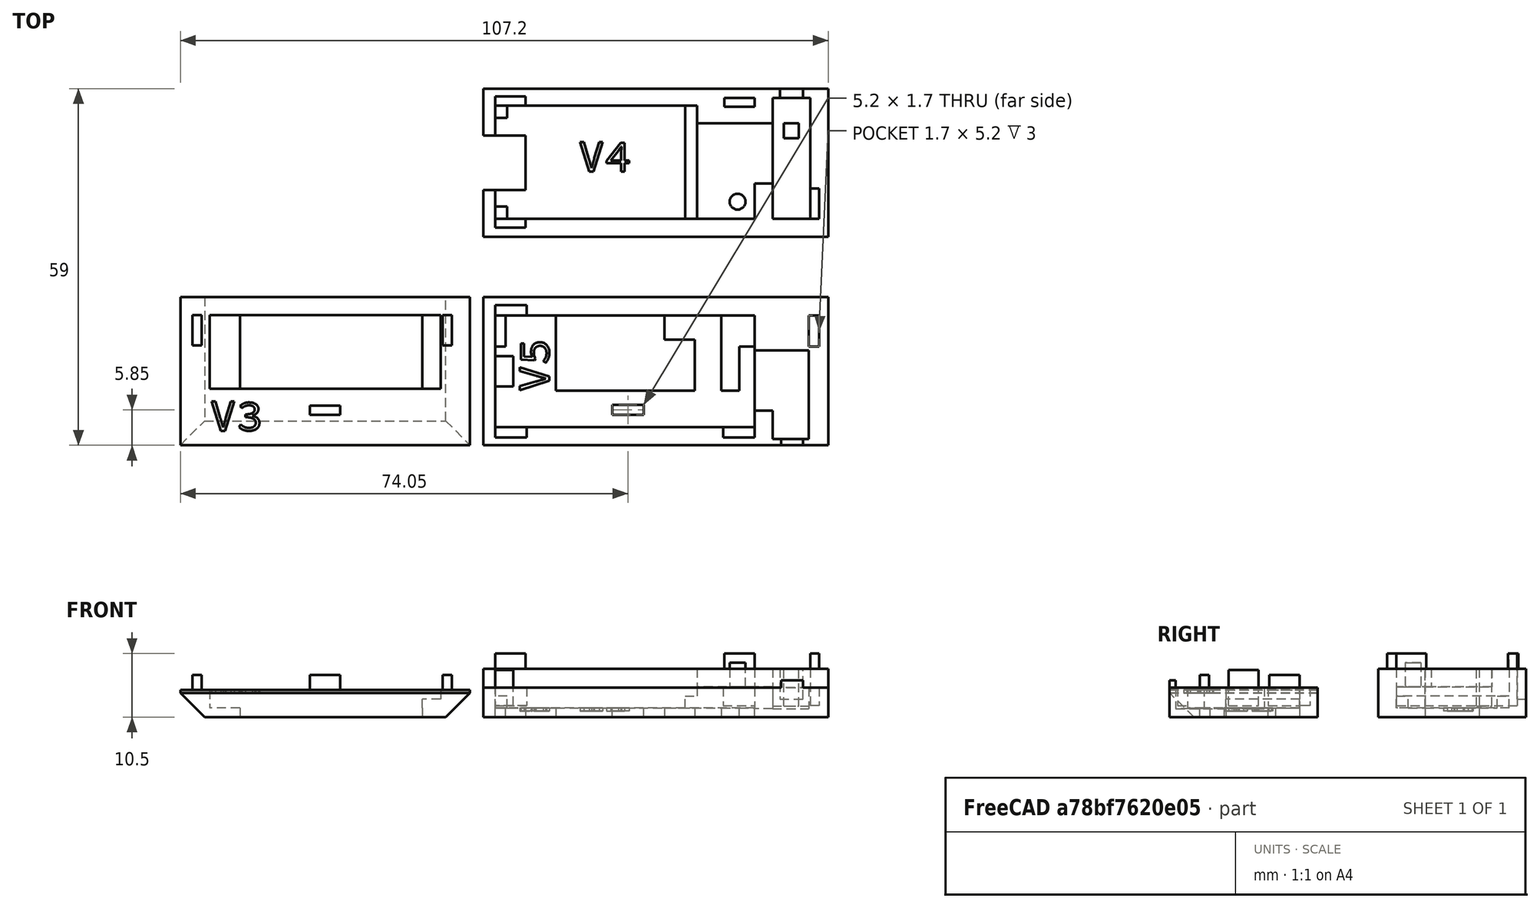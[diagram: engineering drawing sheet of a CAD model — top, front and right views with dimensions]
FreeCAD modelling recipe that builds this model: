
FCSTD DOCUMENT  (FreeCAD 0.18R16161 (Git))
Label: ppm_body
License: All rights reserved
LicenseURL: http://en.wikipedia.org/wiki/All_rights_reserved
objects: Sketcher::SketchObject×29, PartDesign::Pocket×15, PartDesign::Pad×14, App::MeasureDistance×7, Part::Part2DObjectPython×3, Part::Extrusion×3, PartDesign::Body×3, Part::Cut×3, Mesh::Feature×3, PartDesign::Chamfer×1
note: 100 computed .brp shape members not serialized (recipe doc carries the construction recipe); baked Part::Feature solids carry a one-line shape summary decoded from their .brp

FEATURE [Sketcher::SketchObject] Sketch  label="Case_Sketch"
  MapMode = 5
  Support = -> [XY_Plane]
  sketch-geometry (4):
    g0: LineSegment StartX=0 StartY=0 StartZ=0 EndX=47.9 EndY=0 EndZ=0
    g1: LineSegment StartX=47.9 StartY=0 StartZ=0 EndX=47.9 EndY=24.5 EndZ=0
    g2: LineSegment StartX=47.9 StartY=24.5 StartZ=0 EndX=0 EndY=24.5 EndZ=0
    g3: LineSegment StartX=0 StartY=24.5 StartZ=0 EndX=0 EndY=0 EndZ=0
  constraints (11):
    c: Coincident(g0,g1)
    c: Coincident(g1,g2)
    c: Coincident(g2,g3)
    c: Coincident(g3,g0)
    c: Horizontal(g0)
    c: Horizontal(g2)
    c: Vertical(g1)
    c: Vertical(g3)
    c: Coincident(g0,g-1)
    c: DistanceX(g0,g0) = 47.9
    c: DistanceY(g3,g3) = 24.5
FEATURE [PartDesign::Pad] Pad  label="Case"
  Length = 8
  Length2 = 100
  Profile = -> Sketch
  Type = 0
FEATURE [Sketcher::SketchObject] Sketch001  label="ProMicro_Skethc"
  ExternalGeometry = -> [Pad]
  MapMode = 5
  Placement = pos=(0,0,8) rot=(0,0,1;0rad)
  Support = -> [Pad]
  sketch-geometry (6):
    g0: LineSegment StartX=2 StartY=21.7 StartZ=0 EndX=35.4 EndY=21.7 EndZ=0
    g1: LineSegment StartX=35.4 StartY=21.7 StartZ=0 EndX=35.4 EndY=3 EndZ=0
    g2: LineSegment StartX=35.4 StartY=3 StartZ=0 EndX=2 EndY=3 EndZ=0
    g3: LineSegment StartX=2 StartY=3 StartZ=0 EndX=2 EndY=21.7 EndZ=0
    g4: LineSegment [constr] StartX=2 StartY=0 StartZ=0 EndX=2 EndY=3 EndZ=0
    g5: LineSegment [constr] StartX=0 StartY=3 StartZ=0 EndX=2 EndY=3 EndZ=0
  constraints (18):
    c: Coincident(g0,g1)
    c: Coincident(g1,g2)
    c: Coincident(g2,g3)
    c: Coincident(g3,g0)
    c: Horizontal(g0)
    c: Horizontal(g2)
    c: Vertical(g1)
    c: Vertical(g3)
    c: DistanceX(g2,g2) = 33.4
    c: DistanceY(g3,g3) = 18.7
    c: PointOnObject(g4,g-3)
    c: Vertical(g4)
    c: PointOnObject(g5,g-4)
    c: Horizontal(g5)
    c: DistanceX(g5,g5) = 2
    c: DistanceY(g4,g4) = 3
    c: Coincident(g5,g2)
    c: Coincident(g4,g2)
FEATURE [PartDesign::Pocket] Pocket  label="ProMicro"
  BaseFeature = -> Pad
  Length = 6.5
  Length2 = 100
  Profile = -> Sketch001
  Type = 0
FEATURE [Sketcher::SketchObject] Sketch002  label="USBHole"
  ExternalGeometry = -> [Pocket]
  MapMode = 5
  Placement = pos=(0,0,8) rot=(0,0,1;0rad)
  Support = -> [Pocket]
  sketch-geometry (6):
    g0: GeomPoint X=0 Y=12.25 Z=0
    g1: LineSegment StartX=0 StartY=16.75 StartZ=0 EndX=7 EndY=16.75 EndZ=0
    g2: LineSegment StartX=7 StartY=16.75 StartZ=0 EndX=7 EndY=7.75 EndZ=0
    g3: LineSegment StartX=7 StartY=7.75 StartZ=0 EndX=0 EndY=7.75 EndZ=0
    g4: LineSegment StartX=0 StartY=7.75 StartZ=0 EndX=0 EndY=16.75 EndZ=0
    g5: GeomPoint X=0 Y=12.25 Z=0
  constraints (13):
    c: Symmetric(g-3,g-3,g0)
    c: Coincident(g1,g2)
    c: Coincident(g2,g3)
    c: Coincident(g3,g4)
    c: Coincident(g4,g1)
    c: Horizontal(g1)
    c: Horizontal(g3)
    c: Vertical(g2)
    c: Vertical(g4)
    c: Symmetric(g4,g4,g5)
    c: Coincident(g5,g0)
    c: DistanceY(g4,g4) = 9
    c: DistanceX(g3,g3) = 7
FEATURE [PartDesign::Pocket] Pocket001  label="USBHole001"
  BaseFeature = -> Pocket
  Length = 8
  Length2 = 100
  Profile = -> Sketch002
  Type = 0
FEATURE [Sketcher::SketchObject] Sketch003  label="ProMicroRests"
  ExternalGeometry = -> [Pocket001]
  MapMode = 5
  Placement = pos=(0,0,1.5) rot=(0,0,1;0rad)
  Support = -> [Pocket001]
  sketch-geometry (12):
    g0: LineSegment StartX=35.4 StartY=21.7 StartZ=0 EndX=33.4 EndY=21.7 EndZ=0
    g1: LineSegment StartX=33.4 StartY=21.7 StartZ=0 EndX=33.4 EndY=3 EndZ=0
    g2: LineSegment StartX=33.4 StartY=3 StartZ=0 EndX=35.4 EndY=3 EndZ=0
    g3: LineSegment StartX=35.4 StartY=3 StartZ=0 EndX=35.4 EndY=21.7 EndZ=0
    g4: LineSegment StartX=2 StartY=5 StartZ=0 EndX=4 EndY=5 EndZ=0
    g5: LineSegment StartX=4 StartY=5 StartZ=0 EndX=4 EndY=3 EndZ=0
    g6: LineSegment StartX=4 StartY=3 StartZ=0 EndX=2 EndY=3 EndZ=0
    g7: LineSegment StartX=2 StartY=3 StartZ=0 EndX=2 EndY=5 EndZ=0
    g8: LineSegment StartX=4 StartY=21.7 StartZ=0 EndX=4 EndY=19.7 EndZ=0
    g9: LineSegment StartX=2 StartY=21.7 StartZ=0 EndX=4 EndY=21.7 EndZ=0
    g10: LineSegment StartX=4 StartY=19.7 StartZ=0 EndX=2 EndY=19.7 EndZ=0
    g11: LineSegment StartX=2 StartY=19.7 StartZ=0 EndX=2 EndY=21.7 EndZ=0
  constraints (32):
    c: Coincident(g0,g1)
    c: Coincident(g1,g2)
    c: Coincident(g2,g3)
    c: Coincident(g3,g0)
    c: Horizontal(g0)
    c: Horizontal(g2)
    c: Vertical(g1)
    c: DistanceX(g0,g0) = 2
    c: Coincident(g-5,g0)
    c: Coincident(g2,g-5)
    c: Coincident(g4,g5)
    c: Coincident(g5,g6)
    c: Coincident(g6,g7)
    c: Coincident(g7,g4)
    c: Horizontal(g4)
    c: Horizontal(g6)
    c: Vertical(g5)
    c: Vertical(g7)
    c: DistanceX(g4,g4) = 2
    c: Coincident(g-4,g6)
    c: DistanceY(g5,g5) = 2
    c: Coincident(g9,g8)
    c: Coincident(g8,g10)
    c: Coincident(g10,g11)
    c: Coincident(g11,g9)
    c: Horizontal(g9)
    c: Horizontal(g10)
    c: Vertical(g8)
    c: Vertical(g11)
    c: Equal(g4,g9) = 2
    c: Equal(g5,g8) = 2
    c: Coincident(g-3,g9)
FEATURE [PartDesign::Pad] Pad001  label="ProMicroRest"
  BaseFeature = -> Pocket001
  Length = 2
  Length2 = 100
  Profile = -> Sketch003
  Type = 0
FEATURE [Sketcher::SketchObject] Sketch004  label="MPUHole_Sketch"
  ExternalGeometry = -> [Pad001]
  MapMode = 5
  Placement = pos=(0,0,8) rot=(0,0,1;0rad)
  Support = -> [Pad001]
  sketch-geometry (5):
    g0: LineSegment StartX=35.4 StartY=18.8 StartZ=0 EndX=44.9 EndY=18.8 EndZ=0
    g1: LineSegment StartX=44.9 StartY=18.8 StartZ=0 EndX=44.9 EndY=3 EndZ=0
    g2: LineSegment StartX=44.9 StartY=3 StartZ=0 EndX=35.4 EndY=3 EndZ=0
    g3: LineSegment StartX=35.4 StartY=3 StartZ=0 EndX=35.4 EndY=18.8 EndZ=0
    g4: LineSegment [constr] StartX=44.9 StartY=3 StartZ=0 EndX=47.9 EndY=3 EndZ=0
  constraints (14):
    c: Coincident(g0,g1)
    c: Coincident(g1,g2)
    c: Coincident(g2,g3)
    c: Horizontal(g0)
    c: Horizontal(g2)
    c: Vertical(g1)
    c: Vertical(g3)
    c: DistanceY(g1,g1) = 15.8
    c: Coincident(g3,g0)
    c: Coincident(g-3,g2)
    c: Coincident(g4,g1)
    c: PointOnObject(g4,g-4)
    c: Horizontal(g4)
    c: DistanceX(g4,g4) = 3
FEATURE [PartDesign::Pocket] Pocket002  label="MPU_Hole"
  BaseFeature = -> Pad001
  Length = 3
  Length2 = 100
  Profile = -> Sketch004
  Type = 0
FEATURE [Sketcher::SketchObject] Sketch005  label="Pin_Sketch"
  ExternalGeometry = -> [Pocket002]
  MapMode = 5
  Placement = pos=(0,0,5) rot=(0,0,1;0rad)
  Support = -> [Pocket002]
  sketch-geometry (3):
    g0: LineSegment [constr] StartX=42.1 StartY=3 StartZ=0 EndX=42.1 EndY=5.8 EndZ=0
    g1: LineSegment [constr] StartX=44.9 StartY=5.8 StartZ=0 EndX=42.1 EndY=5.8 EndZ=0
    g2: Circle CenterX=42.1 CenterY=5.8 CenterZ=0 NormalX=0 NormalY=0 NormalZ=1 AngleXU=0 Radius=1.3
  constraints (9):
    c: PointOnObject(g0,g-3)
    c: Vertical(g0)
    c: PointOnObject(g1,g-4)
    c: Horizontal(g1)
    c: DistanceX(g1,g1) = 2.8
    c: DistanceY(g0,g0) = 2.8
    c: Coincident(g0,g1)
    c: Radius(g2) = 1.3
    c: Coincident(g2,g0)
FEATURE [PartDesign::Pad] Pad002  label="Pin"
  BaseFeature = -> Pocket002
  Length = 4
  Length2 = 100
  Profile = -> Sketch005
  Type = 0
FEATURE [Sketcher::SketchObject] Sketch006  label="Clips_Sketch"
  ExternalGeometry = -> [Pad002]
  MapMode = 5
  Placement = pos=(0,0,8) rot=(0,0,1;0rad)
  Support = -> [Pad002]
  sketch-geometry (15):
    g0: LineSegment StartX=2 StartY=23.2 StartZ=0 EndX=7 EndY=23.2 EndZ=0
    g1: LineSegment StartX=7 StartY=23.2 StartZ=0 EndX=7 EndY=21.7 EndZ=0
    g2: LineSegment StartX=7 StartY=21.7 StartZ=0 EndX=2 EndY=21.7 EndZ=0
    g3: LineSegment StartX=2 StartY=21.7 StartZ=0 EndX=2 EndY=23.2 EndZ=0
    g4: LineSegment StartX=2 StartY=3 StartZ=0 EndX=7 EndY=3 EndZ=0
    g5: LineSegment StartX=7 StartY=3 StartZ=0 EndX=7 EndY=1.5 EndZ=0
    g6: LineSegment StartX=7 StartY=1.5 StartZ=0 EndX=2 EndY=1.5 EndZ=0
    g7: LineSegment StartX=2 StartY=1.5 StartZ=0 EndX=2 EndY=3 EndZ=0
    g8: GeomPoint X=47.9 Y=12.25 Z=0
    g9: LineSegment StartX=44.9 StartY=23 StartZ=0 EndX=39.9 EndY=23 EndZ=0
    g10: LineSegment StartX=39.9 StartY=23 StartZ=0 EndX=39.9 EndY=21.5 EndZ=0
    g11: LineSegment StartX=39.9 StartY=21.5 StartZ=0 EndX=44.9 EndY=21.5 EndZ=0
    g12: LineSegment StartX=44.9 StartY=21.5 StartZ=0 EndX=44.9 EndY=23 EndZ=0
    g13: GeomPoint X=44.9 Y=22.25 Z=0
    g14: LineSegment [constr] StartX=44.9 StartY=24.5 StartZ=0 EndX=44.9 EndY=23 EndZ=0
  constraints (39):
    c: Coincident(g0,g1)
    c: Coincident(g1,g2)
    c: Coincident(g2,g3)
    c: Coincident(g3,g0)
    c: Horizontal(g0)
    c: Horizontal(g2)
    c: Vertical(g1)
    c: Vertical(g3)
    c: Coincident(g2,g-3)
    c: DistanceY(g3,g3) = 1.5
    c: DistanceX(g0,g0) = 5
    c: Coincident(g4,g5)
    c: Coincident(g5,g6)
    c: Coincident(g6,g7)
    c: Coincident(g7,g4)
    c: Horizontal(g4)
    c: Horizontal(g6)
    c: Vertical(g5)
    c: Vertical(g7)
    c: Equal(g3,g7) = 1.5
    c: Equal(g0,g4) = 5
    c: Coincident(g4,g-4)
    c: Symmetric(g-5,g-5,g8)
    c: Coincident(g9,g10)
    c: Coincident(g10,g11)
    c: Coincident(g11,g12)
    c: Coincident(g12,g9)
    c: Horizontal(g9)
    c: Horizontal(g11)
    c: Vertical(g10)
    c: Vertical(g12)
    c: DistanceX(g9,g9) = 5
    c: DistanceY(g10,g10) = 1.5
    c: Symmetric(g12,g12,g13)
    c: PointOnObject(g14,g-7)
    c: Vertical(g14)
    c: DistanceY(g14,g14) = 1.5
    c: PointOnObject(g-6,g14)
    c: Coincident(g9,g14)
FEATURE [PartDesign::Pad] Pad003  label="Clips"
  BaseFeature = -> Pad002
  Length = 2.5
  Length2 = 100
  Profile = -> Sketch006
  Type = 0
FEATURE [Sketcher::SketchObject] Sketch009  label="Case_Sketch001"
  MapMode = 5
  Support = -> [XY_Plane001]
  sketch-geometry (5):
    g0: LineSegment StartX=0 StartY=-10 StartZ=0 EndX=47.9 EndY=-10 EndZ=0
    g1: LineSegment StartX=47.9 StartY=-10 StartZ=0 EndX=47.9 EndY=-34.5 EndZ=0
    g2: LineSegment StartX=47.9 StartY=-34.5 StartZ=0 EndX=0 EndY=-34.5 EndZ=0
    g3: LineSegment StartX=0 StartY=-34.5 StartZ=0 EndX=0 EndY=-10 EndZ=0
    g4: LineSegment [constr] StartX=0 StartY=0 StartZ=0 EndX=0 EndY=-10 EndZ=0
  constraints (15):
    c: Coincident(g0,g1)
    c: Coincident(g1,g2)
    c: Coincident(g2,g3)
    c: Horizontal(g0)
    c: Horizontal(g2)
    c: Vertical(g1)
    c: Vertical(g3)
    c: DistanceX(g2,g2) = 47.9
    c: DistanceY(g3,g3) = 24.5
    c: Coincident(g0,g3)
    c: PointOnObject(g4,g-1)
    c: Vertical(g4)
    c: DistanceY(g4,g4) = 10
    c: Coincident(g0,g4)
    c: PointOnObject(g0,g-2)
FEATURE [PartDesign::Pad] Pad004  label="Case001"
  Length = 4.9
  Length2 = 100
  Profile = -> Sketch009
  Type = 0
FEATURE [Sketcher::SketchObject] Sketch010  label="Cavity_Sketch"
  ExternalGeometry = -> [Pad004]
  MapMode = 5
  Placement = pos=(0,0,4.9) rot=(0,0,1;0rad)
  Support = -> [Pad004]
  sketch-geometry (8):
    g0: LineSegment StartX=2 StartY=-13 StartZ=0 EndX=44.9 EndY=-13 EndZ=0
    g1: LineSegment StartX=44.9 StartY=-13 StartZ=0 EndX=44.9 EndY=-31.5 EndZ=0
    g2: LineSegment StartX=44.9 StartY=-31.5 StartZ=0 EndX=2 EndY=-31.5 EndZ=0
    g3: LineSegment StartX=2 StartY=-31.5 StartZ=0 EndX=2 EndY=-13 EndZ=0
    g4: LineSegment [constr] StartX=2 StartY=-31.5 StartZ=0 EndX=2 EndY=-34.5 EndZ=0
    g5: LineSegment [constr] StartX=2 StartY=-31.5 StartZ=0 EndX=0 EndY=-31.5 EndZ=0
    g6: LineSegment [constr] StartX=44.9 StartY=-13 StartZ=0 EndX=44.9 EndY=-10 EndZ=0
    g7: LineSegment [constr] StartX=44.9 StartY=-13 StartZ=0 EndX=47.9 EndY=-13 EndZ=0
  constraints (24):
    c: Coincident(g0,g1)
    c: Coincident(g1,g2)
    c: Coincident(g2,g3)
    c: Coincident(g3,g0)
    c: Horizontal(g0)
    c: Horizontal(g2)
    c: Vertical(g1)
    c: Vertical(g3)
    c: Coincident(g4,g2)
    c: PointOnObject(g4,g-4)
    c: Vertical(g4)
    c: Coincident(g5,g2)
    c: PointOnObject(g5,g-5)
    c: Horizontal(g5)
    c: DistanceY(g4,g4) = 3
    c: DistanceX(g5,g5) = 2
    c: Coincident(g6,g0)
    c: PointOnObject(g6,g-6)
    c: Vertical(g6)
    c: DistanceY(g6,g6) = 3
    c: Horizontal(g7)
    c: Coincident(g7,g0)
    c: DistanceX(g7,g7) = 3
    c: PointOnObject(g7,g-3)
FEATURE [PartDesign::Pocket] Pocket005  label="Cavity"
  BaseFeature = -> Pad004
  Length = 3.4
  Length2 = 100
  Profile = -> Sketch010
  Type = 0
FEATURE [Sketcher::SketchObject] Sketch011  label="ClipHoles_Sketch"
  ExternalGeometry = -> [Pocket005]
  MapMode = 5
  Placement = pos=(0,0,4.9) rot=(0,0,1;0rad)
  Support = -> [Pocket005]
  sketch-geometry (12):
    g0: LineSegment StartX=2 StartY=-13 StartZ=0 EndX=7.2 EndY=-13 EndZ=0
    g1: LineSegment StartX=7.2 StartY=-13 StartZ=0 EndX=7.2 EndY=-11.3 EndZ=0
    g2: LineSegment StartX=7.2 StartY=-11.3 StartZ=0 EndX=2 EndY=-11.3 EndZ=0
    g3: LineSegment StartX=2 StartY=-11.3 StartZ=0 EndX=2 EndY=-13 EndZ=0
    g4: LineSegment StartX=2 StartY=-31.5 StartZ=0 EndX=2 EndY=-33.2 EndZ=0
    g5: LineSegment StartX=2 StartY=-33.2 StartZ=0 EndX=7.2 EndY=-33.2 EndZ=0
    g6: LineSegment StartX=7.2 StartY=-33.2 StartZ=0 EndX=7.2 EndY=-31.5 EndZ=0
    g7: LineSegment StartX=7.2 StartY=-31.5 StartZ=0 EndX=2 EndY=-31.5 EndZ=0
    g8: LineSegment StartX=44.9 StartY=-31.5 StartZ=0 EndX=39.7 EndY=-31.5 EndZ=0
    g9: LineSegment StartX=39.7 StartY=-31.5 StartZ=0 EndX=39.7 EndY=-33.2 EndZ=0
    g10: LineSegment StartX=39.7 StartY=-33.2 StartZ=0 EndX=44.9 EndY=-33.2 EndZ=0
    g11: LineSegment StartX=44.9 StartY=-33.2 StartZ=0 EndX=44.9 EndY=-31.5 EndZ=0
  constraints (33):
    c: Coincident(g0,g1)
    c: Coincident(g1,g2)
    c: Coincident(g2,g3)
    c: Coincident(g3,g0)
    c: Horizontal(g0)
    c: Horizontal(g2)
    c: Vertical(g1)
    c: Vertical(g3)
    c: DistanceX(g2,g2) = 5.2
    c: Coincident(g0,g-3)
    c: DistanceY(g1,g1) = 1.7
    c: Coincident(g5,g6)
    c: Coincident(g6,g7)
    c: Coincident(g7,g4)
    c: Coincident(g4,g5)
    c: Horizontal(g5)
    c: Horizontal(g7)
    c: Vertical(g6)
    c: Vertical(g4)
    c: Equal(g2,g7) = 5.2
    c: Equal(g1,g6) = 1.7
    c: Coincident(g4,g-4)
    c: Coincident(g8,g9)
    c: Coincident(g9,g10)
    c: Coincident(g10,g11)
    c: Coincident(g11,g8)
    c: Horizontal(g8)
    c: Horizontal(g10)
    c: Vertical(g9)
    c: Vertical(g11)
    c: Coincident(g-4,g8)
    c: DistanceY(g11,g11) = 1.7
    c: DistanceX(g10,g10) = 5.2
FEATURE [PartDesign::Pocket] Pocket006  label="ClipHoles"
  BaseFeature = -> Pocket005
  Length = 3
  Length2 = 100
  Profile = -> Sketch011
  Type = 0
FEATURE [Part::Part2DObjectPython] ShapeString001  label="TopVersion"  # Draft 2D object (typed FeaturePython)
  FontFile = <userpath>/CAD/SourceCodePro-Regular.otf
  Placement = pos=(10.9786,-25.7002,1.5) rot=(0,0,1;1.5708rad)
  Size = 3
  String = V5
  Tracking = 0
FEATURE [Part::Part2DObjectPython] ShapeString  label="BottomVersion"  # Draft 2D object (typed FeaturePython)
  FontFile = <userpath>/CAD/SourceCodePro-Regular.otf
  Placement = pos=(-12.5,13.82,0) rot=(0,0,1;0rad)
  Size = 3
  String = V4
  Tracking = 0
FEATURE [Part::Extrusion] Extrude  label="BottomVersion "
  Base = -> ShapeString
  Dir = (0,0,-1)
  DirMode = 0
  FaceMakerClass = Part::FaceMakerBullseye
  LengthFwd = 0.5
  LengthRev = 0
  Placement = pos=(28.2223,-3.00852,1.5) rot=(0,0,1;0rad)
  Solid = false
  Symmetric = false
FEATURE [Sketcher::SketchObject] Sketch017  label="Case002_Sketch"
  MapMode = 5
  Support = -> [XY_Plane002]
  sketch-geometry (5):
    g0: LineSegment [constr] StartX=0 StartY=0 StartZ=0 EndX=-10 EndY=0 EndZ=0
    g1: LineSegment StartX=-10 StartY=0 StartZ=0 EndX=-57.9 EndY=0 EndZ=0
    g2: LineSegment StartX=-57.9 StartY=0 StartZ=0 EndX=-57.9 EndY=-24.5 EndZ=0
    g3: LineSegment StartX=-57.9 StartY=-24.5 StartZ=0 EndX=-10 EndY=-24.5 EndZ=0
    g4: LineSegment StartX=-10 StartY=-24.5 StartZ=0 EndX=-10 EndY=0 EndZ=0
  constraints (14):
    c: Coincident(g0,g-1)
    c: PointOnObject(g0,g-1)
    c: DistanceX(g0,g0) = 10
    c: Coincident(g1,g2)
    c: Coincident(g2,g3)
    c: Coincident(g3,g4)
    c: Coincident(g4,g1)
    c: Horizontal(g1)
    c: Horizontal(g3)
    c: Vertical(g2)
    c: Vertical(g4)
    c: Coincident(g1,g0)
    c: DistanceX(g1,g1) = 47.9
    c: DistanceY(g2,g2) = 24.5
FEATURE [PartDesign::Pad] Pad006  label="Case003"
  Length = 4.5
  Length2 = 100
  Profile = -> Sketch017
  Type = 0
FEATURE [Part::Extrusion] Extrude001  label="TopVersion "
  Base = -> ShapeString001
  Dir = (0,0,-1)
  DirMode = 0
  FaceMakerClass = Part::FaceMakerBullseye
  LengthFwd = 0.5
  LengthRev = 0
  Solid = false
  Symmetric = false
FEATURE [Sketcher::SketchObject] Sketch022  label="OledCutout_Sketch"
  ExternalGeometry = -> [Pad006]
  MapMode = 5
  Placement = pos=(0,0,4.5) rot=(0,0,1;0rad)
  Support = -> [Pad006]
  sketch-geometry (9):
    g0: LineSegment StartX=-53.05 StartY=-3 StartZ=0 EndX=-14.85 EndY=-3 EndZ=0
    g1: LineSegment StartX=-14.85 StartY=-3 StartZ=0 EndX=-14.85 EndY=-15.2 EndZ=0
    g2: LineSegment StartX=-14.85 StartY=-15.2 StartZ=0 EndX=-53.05 EndY=-15.2 EndZ=0
    g3: LineSegment StartX=-53.05 StartY=-15.2 StartZ=0 EndX=-53.05 EndY=-3 EndZ=0
    g4: LineSegment [constr] StartX=-53.05 StartY=-3 StartZ=0 EndX=-53.05 EndY=0 EndZ=0
    g5: GeomPoint X=-33.95 Y=-12.25 Z=0
    g6: LineSegment [constr] StartX=-14.85 StartY=-3 StartZ=0 EndX=-10 EndY=-3 EndZ=0
    g7: LineSegment [constr] StartX=-53.05 StartY=-3 StartZ=0 EndX=-57.9 EndY=-3 EndZ=0
    g8: LineSegment [constr] StartX=-53.05 StartY=-15.2 StartZ=0 EndX=-53.05 EndY=-24.5 EndZ=0
  constraints (25):
    c: Coincident(g0,g1)
    c: Coincident(g1,g2)
    c: Coincident(g2,g3)
    c: Coincident(g3,g0)
    c: Horizontal(g0)
    c: Horizontal(g2)
    c: Vertical(g1)
    c: Vertical(g3)
    c: Coincident(g4,g0)
    c: PointOnObject(g4,g-5)
    c: Vertical(g4)
    c: DistanceX(g0,g0) = 38.2
    c: DistanceY(g3,g3) = 12.2
    c: Symmetric(g-5,g-3,g5)
    c: DistanceY(g4,g4) = 3
    c: Coincident(g6,g0)
    c: Coincident(g7,g0)
    c: Horizontal(g7)
    c: PointOnObject(g7,g-3)
    c: PointOnObject(g6,g-4)
    c: Horizontal(g6)
    c: Equal(g6,g7)
    c: Coincident(g8,g2)
    c: Vertical(g8)
    c: PointOnObject(g8,g-6)
FEATURE [PartDesign::Pocket] Pocket015  label="OledCutout"
  BaseFeature = -> Pad006
  Length = 3
  Length2 = 100
  Profile = -> Sketch022
  Type = 0
FEATURE [Sketcher::SketchObject] Sketch023  label="OledScreenWall_Sketch"
  ExternalGeometry = -> [Pocket015]
  MapMode = 5
  Placement = pos=(0,0,1.5) rot=(0,0,1;0rad)
  Support = -> [Pocket015]
  sketch-geometry (6):
    g0: LineSegment [constr] StartX=-53.05 StartY=-3 StartZ=0 EndX=-48.05 EndY=-3 EndZ=0
    g1: LineSegment [constr] StartX=-14.85 StartY=-3 StartZ=0 EndX=-17.85 EndY=-3 EndZ=0
    g2: LineSegment StartX=-17.85 StartY=-3 StartZ=0 EndX=-48.05 EndY=-3 EndZ=0
    g3: LineSegment StartX=-48.05 StartY=-3 StartZ=0 EndX=-48.05 EndY=-15.2 EndZ=0
    g4: LineSegment StartX=-48.05 StartY=-15.2 StartZ=0 EndX=-17.85 EndY=-15.2 EndZ=0
    g5: LineSegment StartX=-17.85 StartY=-15.2 StartZ=0 EndX=-17.85 EndY=-3 EndZ=0
  constraints (16):
    c: Horizontal(g0)
    c: DistanceX(g0,g0) = 5
    c: Coincident(g-3,g0)
    c: Horizontal(g1)
    c: DistanceX(g1,g1) = 3
    c: Coincident(g1,g-4)
    c: Coincident(g2,g3)
    c: Coincident(g3,g4)
    c: Coincident(g4,g5)
    c: Coincident(g5,g2)
    c: Horizontal(g4)
    c: Vertical(g3)
    c: Vertical(g5)
    c: Coincident(g2,g1)
    c: Coincident(g0,g2)
    c: PointOnObject(g3,g-5)
FEATURE [PartDesign::Pocket] Pocket016  label="OledScreenWall"
  BaseFeature = -> Pocket015
  Length = 5
  Length2 = 100
  Profile = -> Sketch023
  Type = 0
FEATURE [Sketcher::SketchObject] Sketch024  label="OledClips_Sketch"
  ExternalGeometry = -> [Pocket016]
  MapMode = 5
  Placement = pos=(0,0,4.5) rot=(0,0,1;0rad)
  Support = -> [Pocket016]
  sketch-geometry (20):
    g0: LineSegment [constr] StartX=-13 StartY=0 StartZ=0 EndX=-13 EndY=-3 EndZ=0
    g1: LineSegment [constr] StartX=-10 StartY=-3 StartZ=0 EndX=-13 EndY=-3 EndZ=0
    g2: LineSegment StartX=-13 StartY=-3 StartZ=0 EndX=-14.5 EndY=-3 EndZ=0
    g3: LineSegment StartX=-14.5 StartY=-3 StartZ=0 EndX=-14.5 EndY=-8 EndZ=0
    g4: LineSegment StartX=-14.5 StartY=-8 StartZ=0 EndX=-13 EndY=-8 EndZ=0
    g5: LineSegment StartX=-13 StartY=-8 StartZ=0 EndX=-13 EndY=-3 EndZ=0
    g6: LineSegment [constr] StartX=-57.9 StartY=-3 StartZ=0 EndX=-55.9 EndY=-3 EndZ=0
    g7: LineSegment StartX=-55.9 StartY=-3 StartZ=0 EndX=-54.4 EndY=-3 EndZ=0
    g8: LineSegment StartX=-54.4 StartY=-3 StartZ=0 EndX=-54.4 EndY=-8 EndZ=0
    g9: LineSegment StartX=-54.4 StartY=-8 StartZ=0 EndX=-55.9 EndY=-8 EndZ=0
    g10: LineSegment StartX=-55.9 StartY=-8 StartZ=0 EndX=-55.9 EndY=-3 EndZ=0
    g11: LineSegment [constr] StartX=-55.9 StartY=-3 StartZ=0 EndX=-55.9 EndY=0 EndZ=0
    g12: LineSegment [constr] StartX=-54.4 StartY=-8 StartZ=0 EndX=-53.05 EndY=-8 EndZ=0
    g13: GeomPoint X=-33.95 Y=-24.5 Z=0
    g14: LineSegment [constr] StartX=-33.95 StartY=-24.5 StartZ=0 EndX=-33.95 EndY=-19.5 EndZ=0
    g15: LineSegment StartX=-36.45 StartY=-18 StartZ=0 EndX=-31.45 EndY=-18 EndZ=0
    g16: LineSegment StartX=-31.45 StartY=-18 StartZ=0 EndX=-31.45 EndY=-19.5 EndZ=0
    g17: LineSegment StartX=-31.45 StartY=-19.5 StartZ=0 EndX=-36.45 EndY=-19.5 EndZ=0
    g18: LineSegment StartX=-36.45 StartY=-19.5 StartZ=0 EndX=-36.45 EndY=-18 EndZ=0
    g19: GeomPoint X=-33.95 Y=-19.5 Z=0
  constraints (54):
    c: PointOnObject(g0,g-3)
    c: Vertical(g0)
    c: DistanceY(g0,g0) = 3
    c: PointOnObject(g1,g-4)
    c: Horizontal(g1)
    c: Coincident(g0,g1)
    c: Coincident(g3,g4)
    c: Coincident(g4,g5)
    c: Coincident(g5,g2)
    c: Horizontal(g4)
    c: Vertical(g3)
    c: Vertical(g5)
    c: Coincident(g2,g0)
    c: DistanceY(g5,g5) = 5
    c: DistanceX(g2,g2) = 1.5
    c: PointOnObject(g6,g-5)
    c: Horizontal(g6)
    c: DistanceX(g6,g6) = 2
    c: Coincident(g7,g8)
    c: Coincident(g8,g9)
    c: Coincident(g9,g10)
    c: Coincident(g10,g7)
    c: Horizontal(g7)
    c: Horizontal(g9)
    c: Vertical(g8)
    c: Vertical(g10)
    c: DistanceX(g7,g7) = 1.5
    c: DistanceY(g10,g10) = 5
    c: Coincident(g6,g7)
    c: Coincident(g11,g7)
    c: PointOnObject(g11,g-3)
    c: DistanceY(g11,g11) = 3
    c: Vertical(g11)
    c: Coincident(g12,g8)
    c: PointOnObject(g12,g-6)
    c: Horizontal(g12)
    c: DistanceX(g1,g1) = 3
    c: Coincident(g3,g2)
    c: Symmetric(g-7,g-7,g13)
    c: Coincident(g14,g13)
    c: Vertical(g14)
    c: DistanceY(g14,g14) = 5
    c: Coincident(g15,g16)
    c: Coincident(g16,g17)
    c: Coincident(g17,g18)
    c: Coincident(g18,g15)
    c: Horizontal(g15)
    c: Horizontal(g17)
    c: Vertical(g16)
    c: Vertical(g18)
    c: DistanceY(g18,g18) = 1.5
    c: DistanceX(g15,g15) = 5
    c: Symmetric(g17,g17,g19)
    c: Coincident(g19,g14)
FEATURE [PartDesign::Pad] Pad007  label="OledClips"
  BaseFeature = -> Pocket016
  Length = 2.5
  Length2 = 100
  Profile = -> Sketch024
  Type = 0
FEATURE [Sketcher::SketchObject] Sketch025  label="ScreenPinPad_Sketch"
  ExternalGeometry = -> [Pad007]
  MapMode = 5
  Placement = pos=(0,0,1.5) rot=(0,0,1;0rad)
  sketch-geometry (4):
    g0: LineSegment StartX=-17.85 StartY=-3 StartZ=0 EndX=-14.85 EndY=-3 EndZ=0
    g1: LineSegment StartX=-14.85 StartY=-3 StartZ=0 EndX=-14.85 EndY=-15.2 EndZ=0
    g2: LineSegment StartX=-14.85 StartY=-15.2 StartZ=0 EndX=-17.85 EndY=-15.2 EndZ=0
    g3: LineSegment StartX=-17.85 StartY=-15.2 StartZ=0 EndX=-17.85 EndY=-3 EndZ=0
  constraints (10):
    c: Coincident(g0,g1)
    c: Coincident(g1,g2)
    c: Coincident(g2,g3)
    c: Coincident(g3,g0)
    c: Horizontal(g0)
    c: Horizontal(g2)
    c: Vertical(g1)
    c: Vertical(g3)
    c: Coincident(g-4,g0)
    c: Coincident(g1,g-3)
FEATURE [Sketcher::SketchObject] Sketch026  label="ProMicroFrontRest_Sketch"
  MapMode = 5
  Placement = pos=(0,0,1.9) rot=(0,0,1;0rad)
  sketch-geometry (7):
    g0: GeomPoint X=0 Y=-22.25 Z=0
    g1: LineSegment [constr] StartX=0 StartY=-22.25 StartZ=0 EndX=2 EndY=-22.25 EndZ=0
    g2: LineSegment StartX=2 StartY=-19.75 StartZ=0 EndX=5 EndY=-19.75 EndZ=0
    g3: LineSegment StartX=5 StartY=-19.75 StartZ=0 EndX=5 EndY=-24.75 EndZ=0
    g4: LineSegment StartX=5 StartY=-24.75 StartZ=0 EndX=2 EndY=-24.75 EndZ=0
    g5: LineSegment StartX=2 StartY=-24.75 StartZ=0 EndX=2 EndY=-19.75 EndZ=0
    g6: GeomPoint X=2 Y=-22.25 Z=0
  constraints (15):
    c: Coincident(g1,g0)
    c: Horizontal(g1)
    c: DistanceX(g1,g1) = 2
    c: Coincident(g2,g3)
    c: Coincident(g3,g4)
    c: Coincident(g4,g5)
    c: Coincident(g5,g2)
    c: Horizontal(g2)
    c: Horizontal(g4)
    c: Vertical(g3)
    c: Vertical(g5)
    c: DistanceY(g3,g3) = 5
    c: DistanceX(g2,g2) = 3
    c: Symmetric(g5,g5,g6)
    c: Coincident(g6,g1)
FEATURE [PartDesign::Pad] Pad009  label="ProMicroFrontRest"
  BaseFeature = -> Pocket006
  Length = 5.9
  Length2 = 100
  Profile = -> Sketch026
  Type = 0
FEATURE [Sketcher::SketchObject] Sketch027  label="ButtonCase_Sketc"
  ExternalGeometry = -> [Pad003]
  MapMode = 5
  Placement = pos=(47.9,0,0) rot=(0.57735,0.57735,0.57735;2.0944rad)
  Support = -> [Pad003]
  sketch-geometry (4):
    g0: LineSegment StartX=0 StartY=8 StartZ=0 EndX=24.5 EndY=8 EndZ=0
    g1: LineSegment StartX=24.5 StartY=8 StartZ=0 EndX=24.5 EndY=0 EndZ=0
    g2: LineSegment StartX=24.5 StartY=0 StartZ=0 EndX=0 EndY=0 EndZ=0
    g3: LineSegment StartX=0 StartY=0 StartZ=0 EndX=0 EndY=8 EndZ=0
  constraints (10):
    c: Coincident(g0,g1)
    c: Coincident(g1,g2)
    c: Coincident(g2,g3)
    c: Coincident(g3,g0)
    c: Horizontal(g0)
    c: Horizontal(g2)
    c: Vertical(g1)
    c: Vertical(g3)
    c: Coincident(g1,g-4)
    c: Coincident(g0,g-3)
FEATURE [PartDesign::Pad] Pad011  label="ButtonCase"
  BaseFeature = -> Pad003
  Length = 9.2
  Length2 = 100
  Profile = -> Sketch027
  Type = 0
FEATURE [Sketcher::SketchObject] Sketch029  label="ButtonCavity_Sketch"
  ExternalGeometry = -> [Pad011]
  MapMode = 5
  Placement = pos=(0,0,8) rot=(0,0,1;0rad)
  Support = -> [Pad011]
  sketch-geometry (7):
    g0: LineSegment StartX=54.1 StartY=23 StartZ=0 EndX=47.9 EndY=23 EndZ=0
    g1: LineSegment StartX=47.9 StartY=23 StartZ=0 EndX=47.9 EndY=3 EndZ=0
    g2: LineSegment StartX=47.9 StartY=3 StartZ=0 EndX=54.1 EndY=3 EndZ=0
    g3: LineSegment StartX=54.1 StartY=3 StartZ=0 EndX=54.1 EndY=23 EndZ=0
    g4: LineSegment [constr] StartX=54.1 StartY=23 StartZ=0 EndX=57.1 EndY=23 EndZ=0
    g5: LineSegment [constr] StartX=54.1 StartY=23 StartZ=0 EndX=54.1 EndY=24.5 EndZ=0
    g6: LineSegment [constr] StartX=47.9 StartY=0 StartZ=0 EndX=47.9 EndY=3 EndZ=0
  constraints (20):
    c: Coincident(g0,g1)
    c: Coincident(g1,g2)
    c: Coincident(g2,g3)
    c: Coincident(g3,g0)
    c: Horizontal(g0)
    c: Horizontal(g2)
    c: Vertical(g1)
    c: Vertical(g3)
    c: Coincident(g4,g0)
    c: Horizontal(g4)
    c: PointOnObject(g4,g-3)
    c: DistanceX(g4,g4) = 3
    c: Coincident(g5,g0)
    c: PointOnObject(g5,g-4)
    c: Vertical(g5)
    c: DistanceY(g5,g5) = 1.5
    c: DistanceX(g2,g2) = 6.2
    c: Coincident(g6,g-5)
    c: Coincident(g6,g1)
    c: DistanceY(g6,g6) = 3
FEATURE [PartDesign::Pocket] Pocket018  label="ButtonCavity"
  BaseFeature = -> Pad011
  Length = 6.2
  Length2 = 100
  Profile = -> Sketch029
  Type = 0
FEATURE [Sketcher::SketchObject] Sketch030  label="ButtonTunnel_Sketch"
  ExternalGeometry = -> [Pocket018]
  MapMode = 5
  Placement = pos=(0,0,8) rot=(0,0,1;0rad)
  Support = -> [Pocket018]
  sketch-geometry (4):
    g0: LineSegment StartX=44.9 StartY=18.8 StartZ=0 EndX=47.9 EndY=18.8 EndZ=0
    g1: LineSegment StartX=47.9 StartY=18.8 StartZ=0 EndX=47.9 EndY=8.8 EndZ=0
    g2: LineSegment StartX=47.9 StartY=8.8 StartZ=0 EndX=44.9 EndY=8.8 EndZ=0
    g3: LineSegment StartX=44.9 StartY=8.8 StartZ=0 EndX=44.9 EndY=18.8 EndZ=0
  constraints (11):
    c: Coincident(g0,g1)
    c: Coincident(g1,g2)
    c: Coincident(g2,g3)
    c: Coincident(g3,g0)
    c: Horizontal(g0)
    c: Horizontal(g2)
    c: Vertical(g1)
    c: Vertical(g3)
    c: DistanceY(g3,g3) = 10
    c: PointOnObject(g0,g-4)
    c: Coincident(g0,g-3)
FEATURE [PartDesign::Pocket] Pocket019  label="ButtonTunnel"
  BaseFeature = -> Pocket018
  Length = 3
  Length2 = 100
  Profile = -> Sketch030
  Type = 0
FEATURE [Sketcher::SketchObject] Sketch031  label="ButtonWall_Sketch"
  ExternalGeometry = -> [Pocket019]
  MapMode = 5
  Placement = pos=(0,23,0) rot=(1,0,0;1.5708rad)
  Support = -> [Pocket019]
  sketch-geometry (7):
    g0: LineSegment [constr] StartX=49.1 StartY=1.8 StartZ=0 EndX=49.1 EndY=3 EndZ=0
    g1: LineSegment [constr] StartX=47.9 StartY=3 StartZ=0 EndX=49.1 EndY=3 EndZ=0
    g2: LineSegment StartX=49.1 StartY=8 StartZ=0 EndX=52.9 EndY=8 EndZ=0
    g3: LineSegment StartX=52.9 StartY=8 StartZ=0 EndX=52.9 EndY=3 EndZ=0
    g4: LineSegment StartX=52.9 StartY=3 StartZ=0 EndX=49.1 EndY=3 EndZ=0
    g5: LineSegment StartX=49.1 StartY=3 StartZ=0 EndX=49.1 EndY=8 EndZ=0
    g6: LineSegment [constr] StartX=52.9 StartY=8 StartZ=0 EndX=54.1 EndY=8 EndZ=0
  constraints (21):
    c: Vertical(g0)
    c: PointOnObject(g0,g-4)
    c: DistanceY(g0,g0) = 1.2
    c: Horizontal(g1)
    c: DistanceX(g1,g1) = 1.2
    c: PointOnObject(g1,g-3)
    c: Coincident(g0,g1)
    c: Coincident(g2,g3)
    c: Coincident(g3,g4)
    c: Coincident(g4,g5)
    c: Coincident(g5,g2)
    c: Horizontal(g2)
    c: Horizontal(g4)
    c: Vertical(g3)
    c: Vertical(g5)
    c: Coincident(g0,g4)
    c: Horizontal(g6)
    c: Equal(g1,g6) = 1.2
    c: Coincident(g2,g6)
    c: PointOnObject(g6,g-5)
    c: PointOnObject(g2,g-6)
FEATURE [PartDesign::Pocket] Pocket020  label="ButtonWall"
  BaseFeature = -> Pocket019
  Length = 5
  Length2 = 100
  Profile = -> Sketch031
  Type = 0
FEATURE [Sketcher::SketchObject] Sketch032  label="ButtonRest_Sketch"
  ExternalGeometry = -> [Pocket020]
  MapMode = 5
  Placement = pos=(0,0,1.8) rot=(0,0,1;0rad)
  Support = -> [Pocket020]
  sketch-geometry (7):
    g0: GeomPoint X=51 Y=23 Z=0
    g1: LineSegment [constr] StartX=51 StartY=23 StartZ=0 EndX=51 EndY=18.8 EndZ=0
    g2: LineSegment StartX=49.75 StartY=18.8 StartZ=0 EndX=52.25 EndY=18.8 EndZ=0
    g3: LineSegment StartX=52.25 StartY=18.8 StartZ=0 EndX=52.25 EndY=16.3 EndZ=0
    g4: LineSegment StartX=52.25 StartY=16.3 StartZ=0 EndX=49.75 EndY=16.3 EndZ=0
    g5: LineSegment StartX=49.75 StartY=16.3 StartZ=0 EndX=49.75 EndY=18.8 EndZ=0
    g6: GeomPoint X=51 Y=18.8 Z=0
  constraints (16):
    c: Symmetric(g-4,g-4,g0)
    c: Coincident(g1,g0)
    c: Vertical(g1)
    c: DistanceY(g1,g1) = 4.2
    c: Coincident(g2,g3)
    c: Coincident(g3,g4)
    c: Coincident(g4,g5)
    c: Coincident(g5,g2)
    c: Horizontal(g2)
    c: Horizontal(g4)
    c: Vertical(g3)
    c: Vertical(g5)
    c: DistanceX(g4,g4) = 2.5
    c: Equal(g4,g3)
    c: Symmetric(g2,g2,g6)
    c: Coincident(g1,g6)
FEATURE [PartDesign::Pad] Pad012  label="ButtonRest"
  BaseFeature = -> Pocket020
  Length = 6.2
  Length2 = 100
  Profile = -> Sketch032
  Type = 0
FEATURE [Sketcher::SketchObject] Sketch033  label="ButtonClip_Sketch"
  ExternalGeometry = -> [Pad012]
  MapMode = 5
  Placement = pos=(0,0,8) rot=(0,0,1;0rad)
  Support = -> [Pad012]
  sketch-geometry (4):
    g0: LineSegment StartX=54.1 StartY=3 StartZ=0 EndX=55.6 EndY=3 EndZ=0
    g1: LineSegment StartX=55.6 StartY=3 StartZ=0 EndX=55.6 EndY=8 EndZ=0
    g2: LineSegment StartX=55.6 StartY=8 StartZ=0 EndX=54.1 EndY=8 EndZ=0
    g3: LineSegment StartX=54.1 StartY=8 StartZ=0 EndX=54.1 EndY=3 EndZ=0
  constraints (11):
    c: Coincident(g0,g1)
    c: Coincident(g1,g2)
    c: Coincident(g2,g3)
    c: Coincident(g3,g0)
    c: Horizontal(g0)
    c: Horizontal(g2)
    c: Vertical(g1)
    c: Vertical(g3)
    c: DistanceX(g0,g0) = 1.5
    c: DistanceY(g1,g1) = 5
    c: Coincident(g-3,g0)
FEATURE [PartDesign::Pad] Pad013  label="ButtonClip"
  BaseFeature = -> Pad012
  Length = 2.5
  Length2 = 100
  Profile = -> Sketch033
  Type = 0
FEATURE [PartDesign::Body] Body  label="Bottom"
  Group = -> [Sketch,Pad,Sketch001,Pocket,Sketch002,Pocket001,Sketch003,Pad001,Sketch004,Pocket002,Sketch005,Pad002,Sketch006,Pad003,Sketch027,Pad011,Sketch029,Pocket018,Sketch030,Pocket019,Sketch031,Pocket020,Sketch032,Pad012,Sketch033,Pad013]
  Origin = -> Origin
  Tip = -> Pad013
FEATURE [Sketcher::SketchObject] Sketch034  label="Button_Sketch"
  ExternalGeometry = -> [Pad009]
  MapMode = 5
  Placement = pos=(47.9,0,0) rot=(0.57735,0.57735,0.57735;2.0944rad)
  Support = -> [Pad009]
  sketch-geometry (4):
    g0: LineSegment StartX=-34.5 StartY=4.9 StartZ=0 EndX=-10 EndY=4.9 EndZ=0
    g1: LineSegment StartX=-10 StartY=4.9 StartZ=0 EndX=-10 EndY=0 EndZ=0
    g2: LineSegment StartX=-10 StartY=0 StartZ=0 EndX=-34.5 EndY=0 EndZ=0
    g3: LineSegment StartX=-34.5 StartY=0 StartZ=0 EndX=-34.5 EndY=4.9 EndZ=0
  constraints (10):
    c: Coincident(g0,g1)
    c: Coincident(g1,g2)
    c: Coincident(g2,g3)
    c: Coincident(g3,g0)
    c: Horizontal(g0)
    c: Horizontal(g2)
    c: Vertical(g1)
    c: Vertical(g3)
    c: Coincident(g1,g-4)
    c: Coincident(g0,g-3)
FEATURE [PartDesign::Pad] Pad014  label="Button"
  BaseFeature = -> Pad009
  Length = 9.2
  Length2 = 100
  Profile = -> Sketch034
  Type = 0
FEATURE [Sketcher::SketchObject] Sketch035  label="ButtonClip_Sketh"
  ExternalGeometry = -> [Pad014]
  MapMode = 5
  Placement = pos=(0,0,4.9) rot=(0,0,1;0rad)
  Support = -> [Pad014]
  sketch-geometry (6):
    g0: LineSegment [constr] StartX=55.6 StartY=-10 StartZ=0 EndX=55.6 EndY=-13 EndZ=0
    g1: LineSegment StartX=55.6 StartY=-13 StartZ=0 EndX=53.9 EndY=-13 EndZ=0
    g2: LineSegment StartX=53.9 StartY=-13 StartZ=0 EndX=53.9 EndY=-18.2 EndZ=0
    g3: LineSegment StartX=53.9 StartY=-18.2 StartZ=0 EndX=55.6 EndY=-18.2 EndZ=0
    g4: LineSegment StartX=55.6 StartY=-18.2 StartZ=0 EndX=55.6 EndY=-13 EndZ=0
    g5: LineSegment [constr] StartX=55.6 StartY=-13 StartZ=0 EndX=57.1 EndY=-13 EndZ=0
  constraints (18):
    c: Vertical(g0)
    c: DistanceY(g0,g0) = 3
    c: PointOnObject(g0,g-3)
    c: Coincident(g1,g2)
    c: Coincident(g2,g3)
    c: Coincident(g3,g4)
    c: Coincident(g4,g1)
    c: Horizontal(g1)
    c: Horizontal(g3)
    c: Vertical(g2)
    c: Vertical(g4)
    c: DistanceY(g4,g4) = 5.2
    c: DistanceX(g3,g3) = 1.7
    c: Coincident(g0,g1)
    c: PointOnObject(g5,g-6)
    c: Horizontal(g5)
    c: Coincident(g5,g1)
    c: DistanceX(g5,g5) = 1.5
FEATURE [PartDesign::Pocket] Pocket021  label="ButtonClip001"
  BaseFeature = -> Pad014
  Length = 3
  Length2 = 100
  Profile = -> Sketch035
  Type = 0
FEATURE [Sketcher::SketchObject] Sketch036  label="ButtonWallClip_Sketch"
  ExternalGeometry = -> [Pocket021]
  MapMode = 5
  Placement = pos=(0,0,4.9) rot=(0,0,1;0rad)
  Support = -> [Pocket021]
  sketch-geometry (5):
    g0: LineSegment StartX=49.3 StartY=-34.5 StartZ=0 EndX=52.9 EndY=-34.5 EndZ=0
    g1: LineSegment StartX=52.9 StartY=-34.5 StartZ=0 EndX=52.9 EndY=-33.5 EndZ=0
    g2: LineSegment StartX=52.9 StartY=-33.5 StartZ=0 EndX=49.3 EndY=-33.5 EndZ=0
    g3: LineSegment StartX=49.3 StartY=-33.5 StartZ=0 EndX=49.3 EndY=-34.5 EndZ=0
    g4: LineSegment [constr] StartX=52.9 StartY=-34.5 StartZ=0 EndX=57.1 EndY=-34.5 EndZ=0
  constraints (14):
    c: Coincident(g0,g1)
    c: Coincident(g1,g2)
    c: Coincident(g2,g3)
    c: Coincident(g3,g0)
    c: Horizontal(g0)
    c: Horizontal(g2)
    c: Vertical(g1)
    c: Vertical(g3)
    c: DistanceX(g2,g2) = 3.6
    c: DistanceY(g3,g3) = 1
    c: Coincident(g4,g0)
    c: Horizontal(g4)
    c: DistanceX(g4,g4) = 4.2
    c: Coincident(g4,g-3)
FEATURE [App::MeasureDistance] Distance003  label="Distance: 5.80 mm"
  Distance = 5.8
  P1 = (44.9,3,8)
  P2 = (44.9,8.8,8)
FEATURE [PartDesign::Pad] Pad016  label="ScreenPinPad"
  BaseFeature = -> Pad007
  Length = 1.5
  Length2 = 100
  Profile = -> Sketch025
  Type = 0
FEATURE [PartDesign::Pad] Pad015  label="ButtonWallClip"
  BaseFeature = -> Pocket021
  Length = 1.2
  Length2 = 100
  Profile = -> Sketch036
  Type = 0
FEATURE [Sketcher::SketchObject] Sketch037  label="ButtonWireCutout_Sketch"
  ExternalGeometry = -> [Pad015]
  MapMode = 5
  Placement = pos=(0,0,4.9) rot=(0,0,1;0rad)
  Support = -> [Pad015]
  sketch-geometry (5):
    g0: LineSegment StartX=44.9 StartY=-18.8 StartZ=0 EndX=47.9 EndY=-18.8 EndZ=0
    g1: LineSegment StartX=47.9 StartY=-18.8 StartZ=0 EndX=47.9 EndY=-28.8 EndZ=0
    g2: LineSegment StartX=47.9 StartY=-28.8 StartZ=0 EndX=44.9 EndY=-28.8 EndZ=0
    g3: LineSegment StartX=44.9 StartY=-18.8 StartZ=0 EndX=44.9 EndY=-28.8 EndZ=0
    g4: LineSegment [constr] StartX=44.9 StartY=-10 StartZ=0 EndX=44.9 EndY=-18.8 EndZ=0
  constraints (15):
    c: Coincident(g0,g1)
    c: Coincident(g1,g2)
    c: Horizontal(g0)
    c: Horizontal(g2)
    c: Vertical(g1)
    c: DistanceY(g2,g0) = 10
    c: DistanceX(g0,g0) = 3
    c: Coincident(g3,g0)
    c: Coincident(g3,g2)
    c: Vertical(g3)
    c: PointOnObject(g0,g-3)
    c: Vertical(g4)
    c: PointOnObject(g4,g-4)
    c: DistanceY(g4,g4) = 8.8
    c: Coincident(g0,g4)
FEATURE [App::MeasureDistance] Distance005  label="Distance: 4.20 mm"
  Distance = 4.2
  P1 = (52.9,24.5,8)
  P2 = (57.1,24.5,8)
FEATURE [App::MeasureDistance] Distance006  label="Distance: 4.20 mm001"
  Distance = 4.19995
  P1 = (52.9,-34.5,4.9)
  P2 = (57.1,-34.5,4.9)
FEATURE [App::MeasureDistance] Distance007  label="Distance: 10.00 mm"
  Distance = 9.99807
  P1 = (44.8993,8.79935,5)
  P2 = (44.8983,18.7974,5)
FEATURE [App::MeasureDistance] Distance  label="Distance: 6.19 mm"
  Distance = 6.19272
  P1 = (47.9044,22.9983,1.8)
  P2 = (54.0971,22.9963,1.8)
FEATURE [App::MeasureDistance] Distance008  label="Distance: 9.20 mm"
  Distance = 9.2
  P1 = (47.9,0,8)
  P2 = (57.1,0,8)
FEATURE [App::MeasureDistance] Distance009  label="Distance: 9.20 mm001"
  Distance = 9.2
  P1 = (47.9,-34.5,4.9)
  P2 = (57.1,-34.5,4.9)
FEATURE [Part::Part2DObjectPython] ShapeString002  label="OledVersion"  # Draft 2D object (typed FeaturePython)
  FontFile = <userpath>/CAD/SourceCodePro-Regular.otf
  MapMode = 5
  Placement = pos=(0,0,4.5) rot=(0,0,1;0rad)
  Size = 3
  String = V3
  Support = -> [Pad016]
  Tracking = 0
FEATURE [Part::Extrusion] Extrude002  label="OledVersion "
  Base = -> ShapeString002
  Dir = (0,0,-1)
  DirMode = 0
  FaceMakerClass = Part::FaceMakerBullseye
  LengthFwd = 0.5
  LengthRev = 0
  Placement = pos=(-45.2399,-32.1437,0) rot=(0,0,1;0rad)
  Solid = false
  Symmetric = false
FEATURE [Part::Cut] Cut001  label="Bottom (Cut)"
  Base = -> Body
  Tool = -> Extrude
FEATURE [PartDesign::Chamfer] Chamfer
  Base = -> Pad016 [Edge9,Edge11,Edge6]
  BaseFeature = -> Pad016
  Size = 4
FEATURE [PartDesign::Body] Body002  label="Oled"
  Group = -> [Sketch017,Pad006,Sketch022,Pocket015,Sketch023,Pocket016,Sketch024,Pad007,Sketch025,Pad016,Chamfer]
  Origin = -> Origin002
  Placement = pos=(7.80021,-9.97702,0) rot=(0,0,1;0rad)
  Tip = -> Chamfer
FEATURE [Part::Cut] Cut002  label="Oled (Cut)"
  Base = -> Body002
  Tool = -> Extrude002
FEATURE [Mesh::Feature] Mesh001  label="Bottom (Cut) (Meshed)"
FEATURE [Mesh::Feature] Mesh002  label="Oled (Cut) (Meshed)"
FEATURE [Mesh::Feature] Mesh  label="Top (Cut) (Meshed)"
FEATURE [PartDesign::Body] Body001  label="Top"
  Group = -> [Sketch009,Pad004,Sketch010,Pocket005,Sketch011,Pocket006,Sketch019,Sketch021,Sketch026,Pad009,Sketch034,Pad014,Sketch035,Pocket021,Sketch036,Pad015,Sketch037,Sketch038,Pocket027,Pocket028,Pocket029,Pocket030]
  Origin = -> Origin001
  Tip = -> Pocket030
FEATURE [Sketcher::SketchObject] Sketch019  label="OledSpace_Sketch"
  ExternalGeometry = -> [Pocket028]
  MapMode = 5
  Placement = pos=(0,0,1.5) rot=(0,0,1;0rad)
  sketch-geometry (15):
    g0: LineSegment [constr] StartX=2 StartY=-13 StartZ=0 EndX=2 EndY=-25.5 EndZ=0
    g1: LineSegment [constr] StartX=2 StartY=-25.5 StartZ=0 EndX=40 EndY=-25.5 EndZ=0
    g2: LineSegment [constr] StartX=2 StartY=-25.5 StartZ=0 EndX=12 EndY=-25.5 EndZ=0
    g3: LineSegment [constr] StartX=40 StartY=-25.5 StartZ=0 EndX=30 EndY=-25.5 EndZ=0
    g4: LineSegment StartX=12 StartY=-25.5 StartZ=0 EndX=35 EndY=-25.5 EndZ=0
    g5: LineSegment StartX=30 StartY=-17 StartZ=0 EndX=30 EndY=-13 EndZ=0
    g6: LineSegment StartX=30 StartY=-13 StartZ=0 EndX=12 EndY=-13 EndZ=0
    g7: LineSegment StartX=12 StartY=-13 StartZ=0 EndX=12 EndY=-25.5 EndZ=0
    g8: LineSegment StartX=30 StartY=-17 StartZ=0 EndX=35 EndY=-17 EndZ=0
    g9: LineSegment StartX=35 StartY=-25.5 StartZ=0 EndX=35 EndY=-17 EndZ=0
    g10: LineSegment StartX=42.4 StartY=-13 StartZ=0 EndX=39.4 EndY=-13 EndZ=0
    g11: LineSegment StartX=39.4 StartY=-13 StartZ=0 EndX=39.4 EndY=-25.5 EndZ=0
    g12: LineSegment StartX=39.4 StartY=-25.5 StartZ=0 EndX=42.4 EndY=-25.5 EndZ=0
    g13: LineSegment StartX=42.4 StartY=-25.5 StartZ=0 EndX=42.4 EndY=-13 EndZ=0
    g14: LineSegment [constr] StartX=42.4 StartY=-25.5 StartZ=0 EndX=44.9 EndY=-25.5 EndZ=0
  constraints (42):
    c: Coincident(g0,g1)
    c: Horizontal(g1)
    c: Vertical(g0)
    c: DistanceX(g1,g1) = 38
    c: Coincident(g2,g0)
    c: DistanceX(g2,g2) = 10
    c: Horizontal(g2)
    c: Coincident(g3,g1)
    c: DistanceX(g3,g3) = 10
    c: Horizontal(g3)
    c: Coincident(g6,g7)
    c: Coincident(g7,g4)
    c: Horizontal(g6)
    c: Vertical(g5)
    c: Vertical(g7)
    c: Coincident(g4,g2)
    c: Horizontal(g8)
    c: DistanceX(g8,g8) = 5
    c: Vertical(g9)
    c: DistanceY(g5,g5) = 4
    c: DistanceY(g0,g0) = 12.5
    c: Coincident(g10,g11)
    c: Coincident(g11,g12)
    c: Coincident(g12,g13)
    c: Coincident(g13,g10)
    c: Horizontal(g10)
    c: Horizontal(g12)
    c: Vertical(g11)
    c: Vertical(g13)
    c: DistanceX(g10,g10) = 3
    c: DistanceY(g9,g9) = 8.5
    c: DistanceX(g4,g4) = 23
    c: Coincident(g8,g5)
    c: Coincident(g9,g8)
    c: Coincident(g6,g5)
    c: Coincident(g9,g4)
    c: Horizontal(g14)
    c: DistanceX(g14,g14) = 2.5
    c: Coincident(g14,g12)
    c: DistanceY(g13,g13) = 12.5
    c: Horizontal(g4)
    c: PointOnObject(g1,g12)
FEATURE [Sketcher::SketchObject] Sketch021  label="OledClip_Sketch"
  ExternalGeometry = -> [Pocket029]
  MapMode = 5
  Placement = pos=(0,0,0) rot=(1,0,0;3.14159rad)
  sketch-geometry (19):
    g0: LineSegment [constr] StartX=0 StartY=13 StartZ=0 EndX=2 EndY=13 EndZ=0
    g1: LineSegment StartX=2 StartY=18.2 StartZ=0 EndX=3.7 EndY=18.2 EndZ=0
    g2: LineSegment StartX=3.7 StartY=18.2 StartZ=0 EndX=3.7 EndY=13 EndZ=0
    g3: LineSegment StartX=3.7 StartY=13 StartZ=0 EndX=2 EndY=13 EndZ=0
    g4: LineSegment StartX=2 StartY=13 StartZ=0 EndX=2 EndY=18.2 EndZ=0
    g5: LineSegment [constr] StartX=2 StartY=10 StartZ=0 EndX=2 EndY=13 EndZ=0
    g6: LineSegment StartX=42.4 StartY=18.2 StartZ=0 EndX=44.9 EndY=18.2 EndZ=0
    g7: LineSegment StartX=44.9 StartY=18.2 StartZ=0 EndX=44.9 EndY=13 EndZ=0
    g8: LineSegment StartX=44.9 StartY=13 StartZ=0 EndX=42.4 EndY=13 EndZ=0
    g9: LineSegment StartX=42.4 StartY=13 StartZ=0 EndX=42.4 EndY=18.2 EndZ=0
    g10: LineSegment [constr] StartX=44.9 StartY=13 StartZ=0 EndX=47.9 EndY=13 EndZ=0
    g11: LineSegment [constr] StartX=44.9 StartY=13 StartZ=0 EndX=44.9 EndY=10 EndZ=0
    g12: GeomPoint X=23.95 Y=34.5 Z=0
    g13: LineSegment StartX=21.35 StartY=27.8 StartZ=0 EndX=26.55 EndY=27.8 EndZ=0
    g14: LineSegment StartX=26.55 StartY=27.8 StartZ=0 EndX=26.55 EndY=29.5 EndZ=0
    g15: LineSegment StartX=26.55 StartY=29.5 StartZ=0 EndX=21.35 EndY=29.5 EndZ=0
    g16: LineSegment StartX=21.35 StartY=29.5 StartZ=0 EndX=21.35 EndY=27.8 EndZ=0
    g17: LineSegment [constr] StartX=23.95 StartY=34.5 StartZ=0 EndX=23.95 EndY=29.5 EndZ=0
    g18: GeomPoint X=23.95 Y=29.5 Z=0
  constraints (48):
    c: Horizontal(g0)
    c: DistanceX(g0,g0) = 2
    c: Coincident(g1,g2)
    c: Coincident(g2,g3)
    c: Coincident(g3,g4)
    c: Coincident(g4,g1)
    c: Horizontal(g1)
    c: Horizontal(g3)
    c: Vertical(g2)
    c: Vertical(g4)
    c: DistanceY(g2,g2) = 5.2
    c: DistanceX(g1,g1) = 1.7
    c: Coincident(g0,g3)
    c: Coincident(g5,g3)
    c: Vertical(g5)
    c: DistanceY(g5,g5) = 3
    c: Coincident(g6,g7)
    c: Coincident(g7,g8)
    c: Coincident(g8,g9)
    c: Coincident(g9,g6)
    c: Horizontal(g6)
    c: Horizontal(g8)
    c: Vertical(g7)
    c: Vertical(g9)
    c: DistanceY(g7,g7) = 5.2
    c: DistanceX(g6,g6) = 2.5
    c: Coincident(g10,g7)
    c: Horizontal(g10)
    c: Coincident(g11,g7)
    c: Vertical(g11)
    c: DistanceY(g11,g11) = 3
    c: DistanceX(g10,g10) = 3
    c: Coincident(g13,g14)
    c: Coincident(g14,g15)
    c: Coincident(g15,g16)
    c: Coincident(g16,g13)
    c: Horizontal(g13)
    c: Horizontal(g15)
    c: Vertical(g14)
    c: Vertical(g16)
    c: DistanceX(g15,g15) = 5.2
    c: DistanceY(g16,g16) = 1.7
    c: Coincident(g17,g12)
    c: Vertical(g17)
    c: DistanceY(g17,g17) = 5
    c: Symmetric(g15,g15,g18)
    c: Coincident(g18,g17)
    c: PointOnObject(g10,g-3)
FEATURE [Sketcher::SketchObject] Sketch038  label="ButtonWireCavity_Sketch"
  ExternalGeometry = -> [Pocket030]
  MapMode = 5
  Placement = pos=(0,0,4.9) rot=(0,0,1;0rad)
  Support = -> [Pocket030]
  sketch-geometry (4):
    g0: LineSegment StartX=49.3 StartY=-33.5 StartZ=0 EndX=55.3 EndY=-33.5 EndZ=0
    g1: LineSegment StartX=55.3 StartY=-33.5 StartZ=0 EndX=55.3 EndY=-18.8 EndZ=0
    g2: LineSegment StartX=55.3 StartY=-18.8 StartZ=0 EndX=49.3 EndY=-18.8 EndZ=0
    g3: LineSegment StartX=49.3 StartY=-18.8 StartZ=0 EndX=49.3 EndY=-33.5 EndZ=0
  constraints (11):
    c: Coincident(g0,g1)
    c: Coincident(g1,g2)
    c: Horizontal(g0)
    c: Horizontal(g2)
    c: Vertical(g1)
    c: Coincident(g3,g2)
    c: Coincident(g3,g0)
    c: Vertical(g3)
    c: DistanceX(g2,g2) = 6
    c: DistanceY(g3,g3) = 14.7
    c: Coincident(g-3,g0)
FEATURE [PartDesign::Pocket] Pocket027  label="ButtonWireCavity"
  BaseFeature = -> Pad015
  Length = 3.5
  Length2 = 100
  Profile = -> Sketch038
  Type = 0
FEATURE [PartDesign::Pocket] Pocket028  label="ButtonWireCutout"
  BaseFeature = -> Pocket027
  Length = 3.5
  Length2 = 100
  Profile = -> Sketch037
  Type = 0
FEATURE [PartDesign::Pocket] Pocket029  label="OledSpace"
  BaseFeature = -> Pocket028
  Length = 5
  Length2 = 100
  Profile = -> Sketch019
  Type = 0
FEATURE [PartDesign::Pocket] Pocket030  label="OledClip"
  BaseFeature = -> Pocket029
  Length = 5
  Length2 = 100
  Profile = -> Sketch021
  Type = 0
FEATURE [Part::Cut] Cut  label="Top (Cut)"
  Base = -> Body001
  Tool = -> Extrude001
